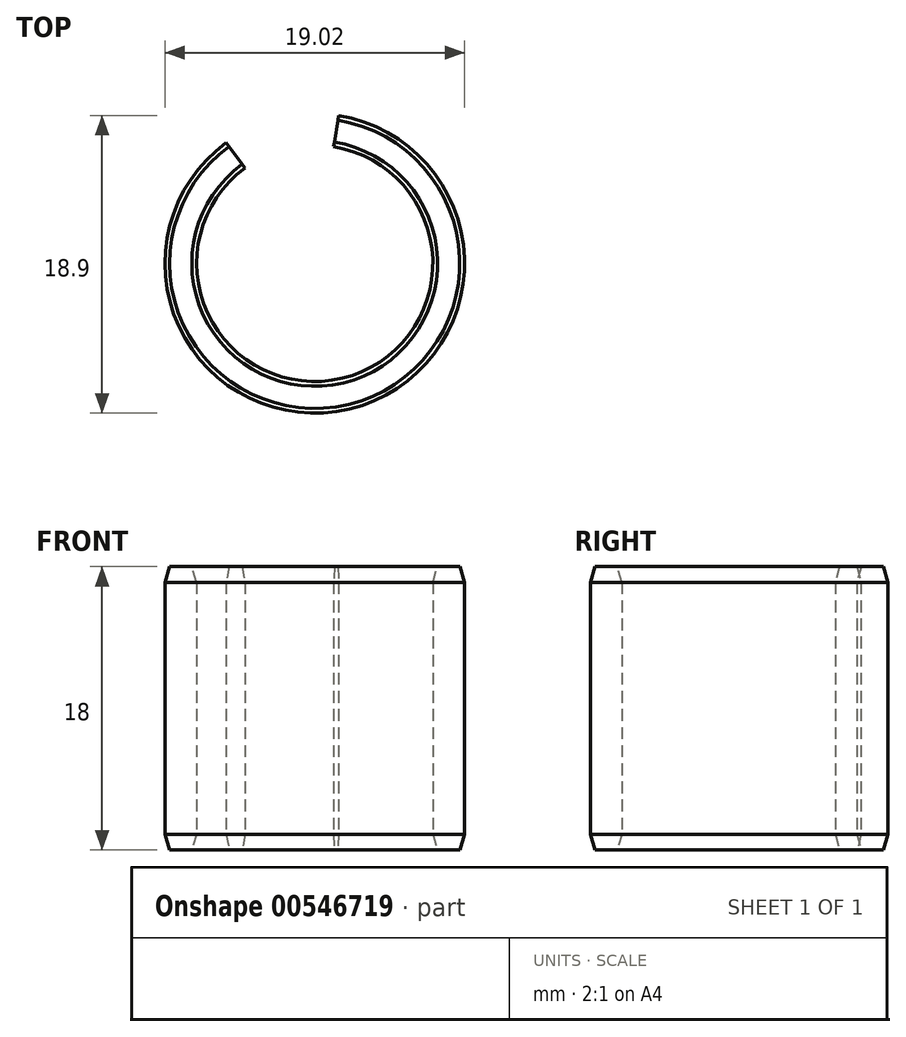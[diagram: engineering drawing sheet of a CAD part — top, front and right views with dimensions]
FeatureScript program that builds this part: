
annotation { "Feature Type Name" : "Feature", "Feature Type Description" : "" }
export const myFeature = defineFeature(function(context is Context, id is Id, definition is map)
    precondition{}
    {
        {
            var Q0;
            Q0=qCreatedBy(makeId("Top.planeOp"),FACE);
            var sketch = newSketch(context, id + "F0", { "sketchPlane" : qUnion([Q0])});
            skArc(sketch, "E0", {"start": v(-4.43, 6.05) * mm, "mid": v(1.75, -7.3) * mm, "end": v(1.2, 7.4) * mm});
            skLineSegment(sketch, "E1", {"start": v(1.2, 7.4) * mm, "end": v(1.53, 9.39) * mm});
            skLineSegment(sketch, "E2", {"start": v(1.53, 9.39) * mm, "end": v(1.2, 7.4) * mm});
            skLineSegment(sketch, "E3", {"start": v(-4.43, 6.05) * mm, "end": v(-5.62, 7.67) * mm});
            skArc(sketch, "E4", {"start": v(-5.57, 7.7) * mm, "mid": v(2.2, -9.26) * mm, "end": v(1.53, 9.39) * mm});
            skSolve(sketch);
        }
        {
            var Q0;
            Q0=makeQuery(id+"F0.imprint","IMPRINT",FACE,{"disambiguationData":[TD([[makeQuery(id+"F0.imprint","IMPRINT",EDGE,{"derivedFrom":sQuery(id+"F0.wireOp",EDGE,"hwYp1XFJ-IAKx-kGjD-dP25-y8G7ijmlLeJh")}),-1.0]])]});
            var Q1;
            Q1=makeQuery(id+"F0.imprint","IMPRINT",FACE,{"disambiguationData":[TD([[makeQuery(id+"F0.imprint","IMPRINT",EDGE,{"derivedFrom":sQuery(id+"F0.wireOp",EDGE,"E0")}),-1.0]])]});
            extrude(context, id + "F1", {"entities" : qUnion([Q0, Q1]), "depth" : 18 * mm, "offsetDistance" : 25 * mm});
        }
        {
            var Q0;
            Q0=makeQuery(id+"F1.opExtrude","CAP_EDGE",EDGE,{"disambiguationData":[OSD([sQuery(id+"F0.wireOp",EDGE,"E4")])],"isStart":false});
            var Q1;
            Q1=makeQuery(id+"F1.opExtrude","CAP_EDGE",EDGE,{"disambiguationData":[OSD([sQuery(id+"F0.wireOp",EDGE,"E0")])],"isStart":false});
            var Q2;
            Q2=makeQuery(id+"F1.opExtrude","CAP_EDGE",EDGE,{"disambiguationData":[OSD([sQuery(id+"F0.wireOp",EDGE,"E4")])],"isStart":true});
            var Q3;
            Q3=makeQuery(id+"F1.opExtrude","CAP_EDGE",EDGE,{"disambiguationData":[OSD([sQuery(id+"F0.wireOp",EDGE,"E0")])],"isStart":true});
            chamfer(context, id + "F2", {"entities" : qUnion([Q0, Q1, Q2, Q3]), "chamferType" : ChamferType.TWO_OFFSETS, "width1" : 0.3 * mm, "oppositeDirection" : false, "width2" : 1 * mm, "tangentPropagation" : true});
        }
    });
